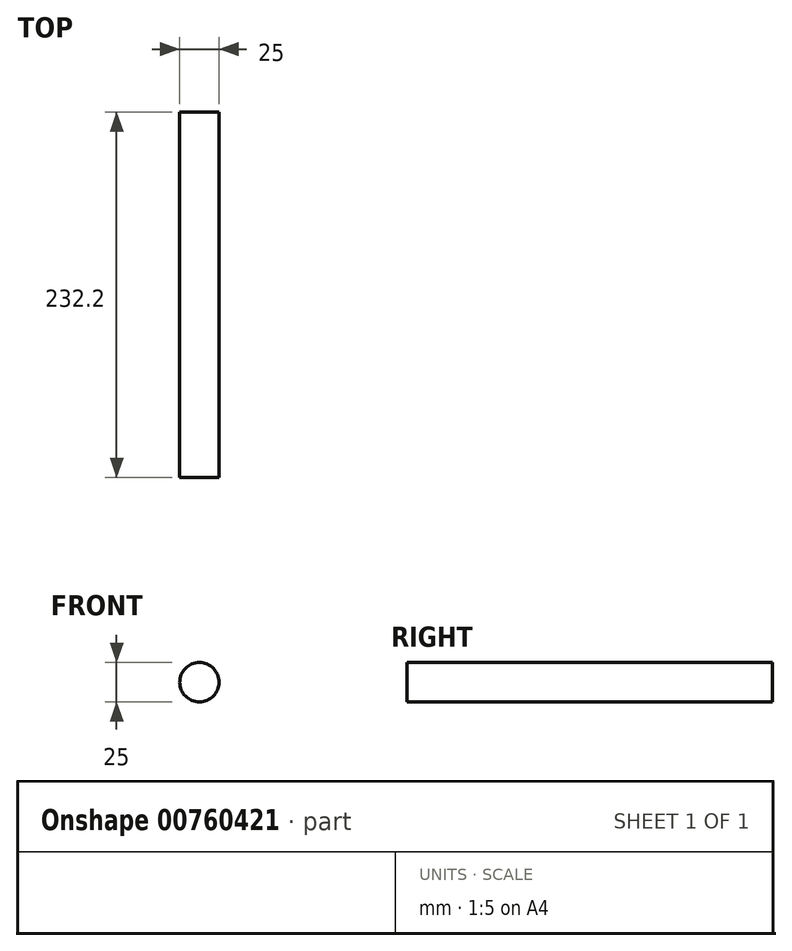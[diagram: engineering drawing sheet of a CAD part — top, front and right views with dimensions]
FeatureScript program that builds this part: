
annotation { "Feature Type Name" : "Feature", "Feature Type Description" : "" }
export const myFeature = defineFeature(function(context is Context, id is Id, definition is map)
    precondition{}
    {
        {
            assignVariable(context, id + "F0", {"name" : "MASS", "anyValue" : 120});
        }
        {
            var Q0;
            Q0=qCreatedBy(makeId("Front.planeOp"),FACE);
            var sketch = newSketch(context, id + "F1", { "sketchPlane" : qUnion([Q0])});
            skCircle(sketch, "E0", {"center": v(0, 0) * mm, "radius": 12.5 * mm});
            skSolve(sketch);
        }
        {
            var Q0;
            Q0=makeQuery(id+"F1.imprint","IMPRINT",FACE,{"disambiguationData":[TD([[makeQuery(id+"F1.imprint","IMPRINT",EDGE,{"derivedFrom":sQuery(id+"F1.wireOp",EDGE,"E0")}),1.0]])]});
            extrude(context, id + "F2", {"entities" : qUnion([Q0]), "endBound" : BoundingType.SYMMETRIC, "depth" : (getVariable(context, 'MASS') * 1.94) * mm, "offsetDistance" : 25 * mm});
        }
    });
